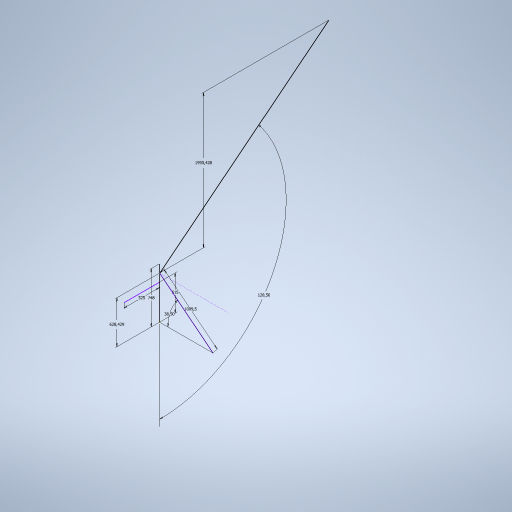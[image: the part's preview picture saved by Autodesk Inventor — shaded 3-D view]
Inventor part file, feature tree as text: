
AUTODESK INVENTOR PART (.ipt)
format: ipt  version: 2024 (Build 280153000, 153)  size: 240,128 bytes
history: native  units: mm
features: sketch x2
ambient origin geometry x8: Origin, YZ Plane, XZ Plane, XY Plane, X Axis, Y Axis, Z Axis, Center Point
feature tree (2):
  sketch  "Sketch1"  dims[d0=525.0mm]
  sketch  "Sketch3"  dims[d1=748.0mm d2=515.0mm d3=1009.5mm d9=6.719518mm d11=628.429mm d12=1990.428299mm d13=22.427481mm]
